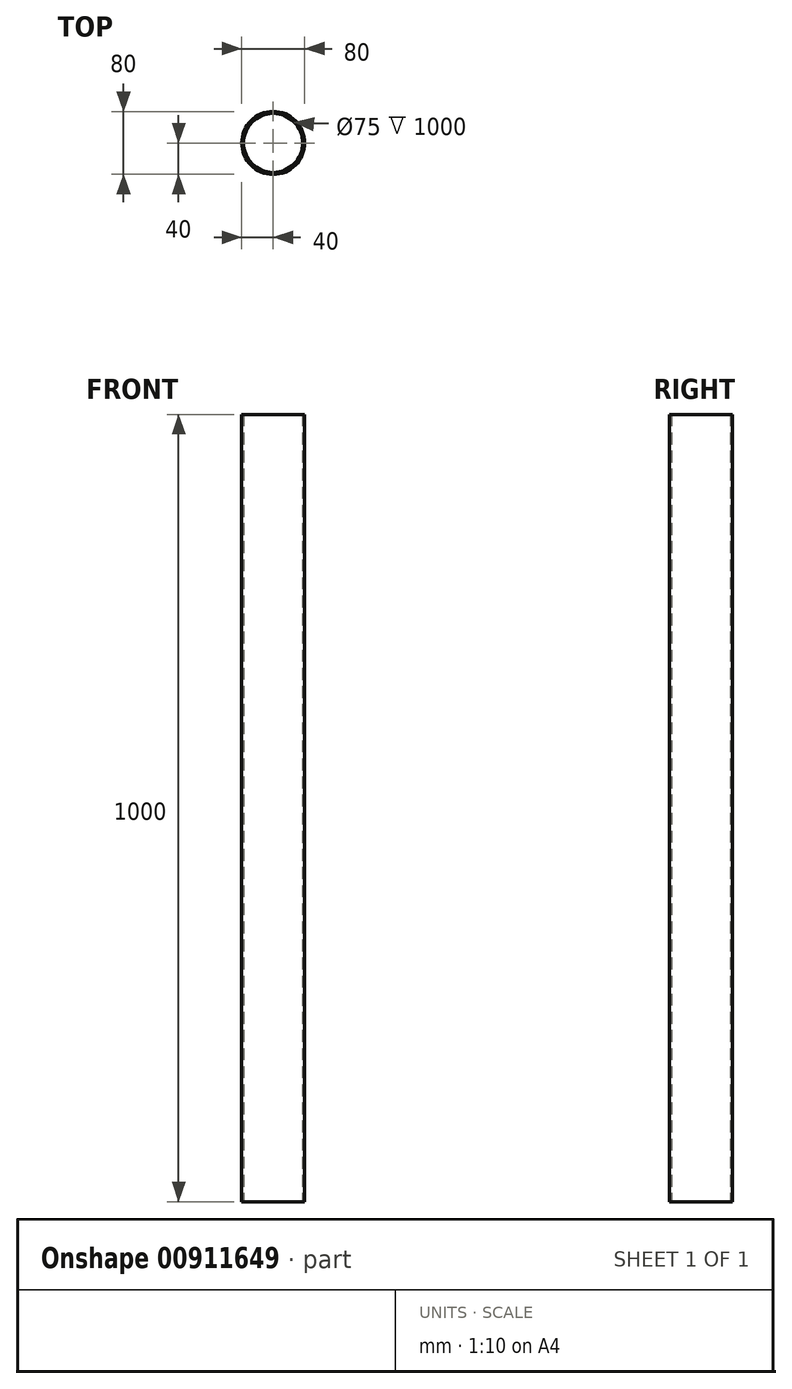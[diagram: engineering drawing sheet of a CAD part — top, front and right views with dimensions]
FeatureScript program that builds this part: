
annotation { "Feature Type Name" : "Feature", "Feature Type Description" : "" }
export const myFeature = defineFeature(function(context is Context, id is Id, definition is map)
    precondition{}
    {
        {
            var Q0;
            Q0=qCreatedBy(makeId("Top.planeOp"),FACE);
            var sketch = newSketch(context, id + "F0", { "sketchPlane" : qUnion([Q0])});
            skCircle(sketch, "E0", {"center": v(0, 0) * mm, "radius": 40 * mm});
            skCircle(sketch, "E1", {"center": v(0, 0) * mm, "radius": 37.5 * mm});
            skSolve(sketch);
        }
        {
            var Q0;
            Q0 = qSketchRegion(id + "F0", true);
            extrude(context, id + "F1", {"entities" : qUnion([Q0]), "depth" : 1000 * mm, "offsetDistance" : 25 * mm});
        }
    });
